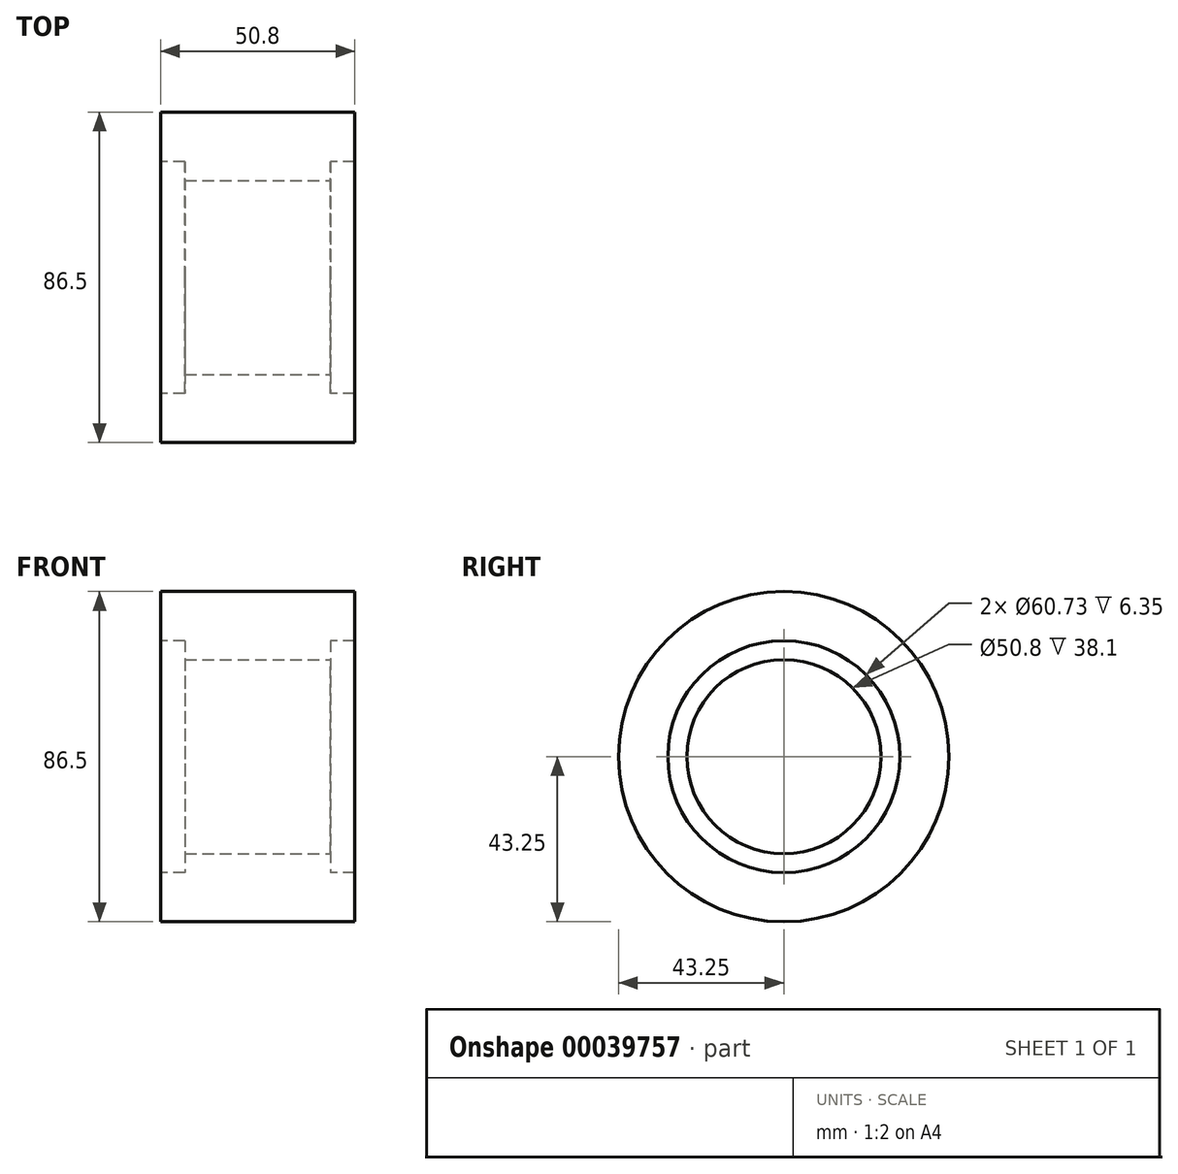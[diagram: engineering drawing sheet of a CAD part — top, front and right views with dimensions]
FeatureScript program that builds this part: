
annotation { "Feature Type Name" : "Feature", "Feature Type Description" : "" }
export const myFeature = defineFeature(function(context is Context, id is Id, definition is map)
    precondition{}
    {
        {
            var Q0;
            Q0=qCreatedBy(makeId("Front.planeOp"),FACE);
            var sketch = newSketch(context, id + "F0", { "sketchPlane" : qUnion([Q0])});
            skLineSegment(sketch, "E0.bottom", {"start": v(0, 0) * mm, "end": v(38.1, 0) * mm});
            skLineSegment(sketch, "E0.top", {"start": v(0, 36.8) * mm, "end": v(38.1, 36.8) * mm});
            skLineSegment(sketch, "E0.left", {"start": v(0, 0) * mm, "end": v(0, 36.8) * mm});
            skLineSegment(sketch, "E0.right", {"start": v(38.1, 0) * mm, "end": v(38.1, 36.8) * mm});
            skLineSegment(sketch, "E1.rect.bottom", {"start": v(44.45, 43.25) * mm, "end": v(-6.35, 43.25) * mm});
            skLineSegment(sketch, "E1.rect.top", {"start": v(44.45, 30.37) * mm, "end": v(-6.35, 30.37) * mm});
            skLineSegment(sketch, "E1.rect.left", {"start": v(44.45, 43.25) * mm, "end": v(44.45, 30.37) * mm});
            skLineSegment(sketch, "E1.rect.right", {"start": v(-6.35, 43.25) * mm, "end": v(-6.35, 30.37) * mm});
            skPoint(sketch, "E1.rect.middle", {"position": v(19.05, 36.8) * mm});
            skSolve(sketch);
        }
        {
            var Q0;
            Q0 = qSketchRegion(id + "F0", true);
            var Q1;
            Q1=sQuery(id+"F0.wireOp",EDGE,"E0.bottom");
            revolve(context, id + "F1", {"entities" : qUnion([Q0]), "axis" : qUnion([Q1]), "revolveType" : RevolveType.FULL});
        }
        {
            var Q0;
            Q0=makeQuery(id+"F1.opRevolve","SWEPT_FACE",FACE,{"disambiguationData":[OSD([sQuery(id+"F0.wireOp",EDGE,"E0.right")])]});
            var sketch = newSketch(context, id + "F2", { "sketchPlane" : qUnion([Q0])});
            skCircle(sketch, "E2", {"center": v(0, 0) * mm, "radius": 25.4 * mm});
            skSolve(sketch);
        }
        {
            var Q0;
            Q0 = qSketchRegion(id + "F2", true);
            extrude(context, id + "F3", {"entities" : qUnion([Q0]), "operationType" : NewBodyOperationType.REMOVE, "endBound" : BoundingType.THROUGH_ALL, "oppositeDirection" : true, "depth" : 25.4 * mm});
        }
    });
